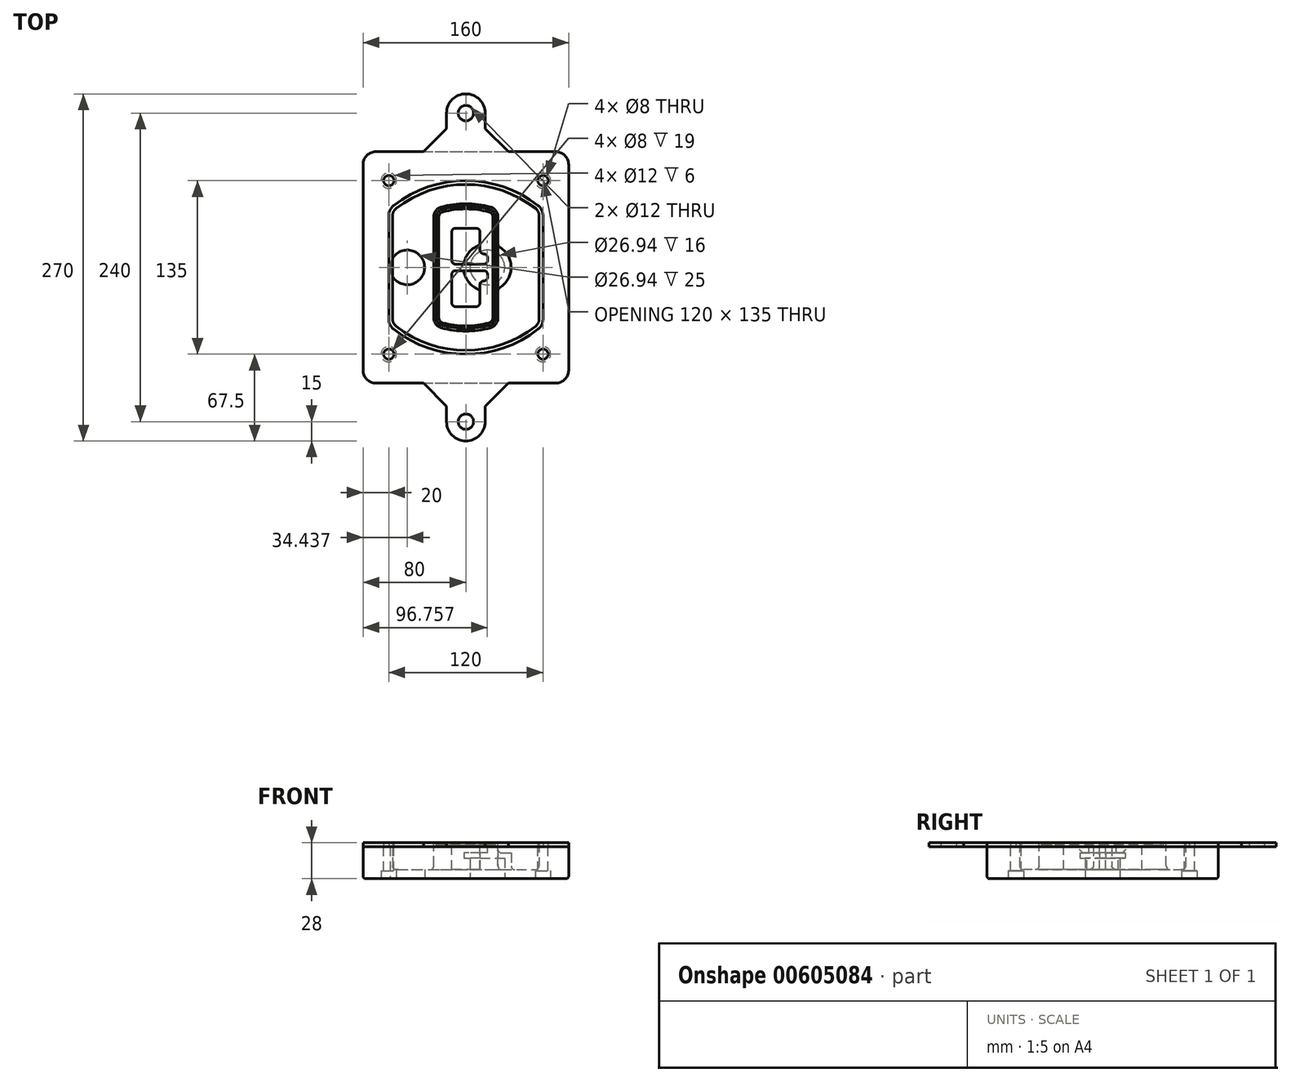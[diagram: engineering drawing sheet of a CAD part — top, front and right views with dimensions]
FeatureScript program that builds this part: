
annotation { "Feature Type Name" : "Feature", "Feature Type Description" : "" }
export const myFeature = defineFeature(function(context is Context, id is Id, definition is map)
    precondition{}
    {
        {
            var Q0;
            Q0=qCreatedBy(makeId("Top.planeOp"),FACE);
            var sketch = newSketch(context, id + "F0", { "sketchPlane" : qUnion([Q0])});
            skPoint(sketch, "E0.rect.middle", {"position": v(0, 0) * mm});
            skLineSegment(sketch, "E1.bottom", {"start": v(-70, -90) * mm, "end": v(70, -90) * mm});
            skLineSegment(sketch, "E1.top", {"start": v(-70, 90) * mm, "end": v(70, 90) * mm});
            skLineSegment(sketch, "E1.left", {"start": v(-80, -80) * mm, "end": v(-80, 80) * mm});
            skLineSegment(sketch, "E1.right", {"start": v(80, -80) * mm, "end": v(80, 80) * mm});
            skLineSegment(sketch, "E2", {"start": v(-80, 90) * mm, "end": v(80, -90) * mm, "construction": true});
            skLineSegment(sketch, "E3", {"start": v(80, 90) * mm, "end": v(-80, -90) * mm, "construction": true});
            skCircle(sketch, "E4", {"center": v(-60, 67.5) * mm, "radius": 4 * mm});
            skCircle(sketch, "E5", {"center": v(60, 67.5) * mm, "radius": 4 * mm});
            skCircle(sketch, "E6", {"center": v(60, -67.5) * mm, "radius": 4 * mm});
            skCircle(sketch, "E7", {"center": v(-60, -67.5) * mm, "radius": 4 * mm});
            skLineSegment(sketch, "E8", {"start": v(-60, 67.5) * mm, "end": v(60, 67.5) * mm, "construction": true});
            skLineSegment(sketch, "E9", {"start": v(60, 67.5) * mm, "end": v(60, -67.5) * mm, "construction": true});
            skLineSegment(sketch, "E10", {"start": v(60, -67.5) * mm, "end": v(-60, -67.5) * mm, "construction": true});
            skLineSegment(sketch, "E11", {"start": v(-60, -67.5) * mm, "end": v(-60, 67.5) * mm, "construction": true});
            skLineSegment(sketch, "E12", {"start": v(-60, 40.3) * mm, "end": v(-60, -40.3) * mm});
            skLineSegment(sketch, "E13", {"start": v(60, 40.3) * mm, "end": v(60, -40.3) * mm});
            skArc(sketch, "E14", {"start": v(56.15, 48.18) * mm, "mid": v(0, 67.5) * mm, "end": v(-56.15, 48.18) * mm});
            skArc(sketch, "E15", {"start": v(-56.15, -48.18) * mm, "mid": v(0, -67.5) * mm, "end": v(56.15, -48.18) * mm});
            skLineSegment(sketch, "E16", {"start": v(-60, 0) * mm, "end": v(60, 0) * mm, "construction": true});
            skPoint(sketch, "E17.visualSharp", {"position": v(-60, -45) * mm});
            skArc(sketch, "E17.filletArc", {"start": v(-60, -40.3) * mm, "mid": v(-58.99, -44.68) * mm, "end": v(-56.15, -48.18) * mm});
            skPoint(sketch, "E18.visualSharp", {"position": v(-60, 45) * mm});
            skArc(sketch, "E18.filletArc", {"start": v(-56.15, 48.18) * mm, "mid": v(-58.99, 44.68) * mm, "end": v(-60, 40.3) * mm});
            skPoint(sketch, "E19.visualSharp", {"position": v(60, 45) * mm});
            skArc(sketch, "E19.filletArc", {"start": v(60, 40.3) * mm, "mid": v(58.99, 44.68) * mm, "end": v(56.15, 48.18) * mm});
            skPoint(sketch, "E20.visualSharp", {"position": v(60, -45) * mm});
            skArc(sketch, "E20.filletArc", {"start": v(56.15, -48.18) * mm, "mid": v(58.99, -44.68) * mm, "end": v(60, -40.3) * mm});
            skPoint(sketch, "E21.visualSharp", {"position": v(-80, 90) * mm});
            skArc(sketch, "E21.filletArc", {"start": v(-70, 90) * mm, "mid": v(-77.07, 87.07) * mm, "end": v(-80, 80) * mm});
            skPoint(sketch, "E22.visualSharp", {"position": v(80, 90) * mm});
            skArc(sketch, "E22.filletArc", {"start": v(80, 80) * mm, "mid": v(77.07, 87.07) * mm, "end": v(70, 90) * mm});
            skPoint(sketch, "E23.visualSharp", {"position": v(80, -90) * mm});
            skArc(sketch, "E23.filletArc", {"start": v(70, -90) * mm, "mid": v(77.07, -87.07) * mm, "end": v(80, -80) * mm});
            skPoint(sketch, "E24.visualSharp", {"position": v(-80, -90) * mm});
            skArc(sketch, "E24.filletArc", {"start": v(-80, -80) * mm, "mid": v(-77.07, -87.07) * mm, "end": v(-70, -90) * mm});
            skArc(sketch, "E25.0", {"start": v(57, 40.3) * mm, "mid": v(56.3, 43.36) * mm, "end": v(54.3, 45.81) * mm});
            skLineSegment(sketch, "E25.1", {"start": v(57, 40.3) * mm, "end": v(57, -40.3) * mm});
            skArc(sketch, "E25.2", {"start": v(54.3, -45.81) * mm, "mid": v(56.3, -43.36) * mm, "end": v(57, -40.3) * mm});
            skArc(sketch, "E25.3", {"start": v(-54.3, -45.81) * mm, "mid": v(0, -64.5) * mm, "end": v(54.3, -45.81) * mm});
            skArc(sketch, "E25.4", {"start": v(-57, -40.3) * mm, "mid": v(-56.3, -43.36) * mm, "end": v(-54.3, -45.81) * mm});
            skArc(sketch, "E25.5", {"start": v(54.3, 45.81) * mm, "mid": v(0, 64.5) * mm, "end": v(-54.3, 45.81) * mm});
            skLineSegment(sketch, "E25.6", {"start": v(-57, 40.3) * mm, "end": v(-57, -40.3) * mm});
            skArc(sketch, "E25.7", {"start": v(-54.3, 45.81) * mm, "mid": v(-56.3, 43.36) * mm, "end": v(-57, 40.3) * mm});
            skArc(sketch, "E26.0", {"start": v(-58.62, 51.33) * mm, "mid": v(-62.58, 46.43) * mm, "end": v(-64, 40.3) * mm});
            skArc(sketch, "E26.1", {"start": v(58.62, 51.33) * mm, "mid": v(0, 71.5) * mm, "end": v(-58.62, 51.33) * mm});
            skArc(sketch, "E26.2", {"start": v(64, 40.3) * mm, "mid": v(62.58, 46.43) * mm, "end": v(58.62, 51.33) * mm});
            skLineSegment(sketch, "E26.3", {"start": v(64, 40.3) * mm, "end": v(64, -40.3) * mm});
            skArc(sketch, "E26.4", {"start": v(58.62, -51.33) * mm, "mid": v(62.58, -46.43) * mm, "end": v(64, -40.3) * mm});
            skLineSegment(sketch, "E26.5", {"start": v(-64, 40.3) * mm, "end": v(-64, -40.3) * mm});
            skArc(sketch, "E26.6", {"start": v(-58.62, -51.33) * mm, "mid": v(0, -71.5) * mm, "end": v(58.62, -51.33) * mm});
            skArc(sketch, "E26.7", {"start": v(-64, -40.3) * mm, "mid": v(-62.58, -46.43) * mm, "end": v(-58.62, -51.33) * mm});
            skSolve(sketch);
        }
        {
            var Q0;
            Q0=makeQuery(id+"F0.imprint","IMPRINT",FACE,{"disambiguationData":[TD([[makeQuery(id+"F0.imprint","IMPRINT",EDGE,{"derivedFrom":sQuery(id+"F0.wireOp",EDGE,"E1.bottom")}),1.0]])]});
            var Q1;
            Q1=makeQuery(id+"F0.imprint","IMPRINT",FACE,{"disambiguationData":[TD([[makeQuery(id+"F0.imprint","IMPRINT",EDGE,{"derivedFrom":sQuery(id+"F0.wireOp",EDGE,"E12")}),1.0]])]});
            var Q2;
            Q2=makeQuery(id+"F0.imprint","IMPRINT",FACE,{"disambiguationData":[TD([[makeQuery(id+"F0.imprint","IMPRINT",EDGE,{"derivedFrom":sQuery(id+"F0.wireOp",EDGE,"E25.0")}),1.0]])]});
            var Q3;
            Q3=makeQuery(id+"F0.imprint","IMPRINT",FACE,{"disambiguationData":[TD([[makeQuery(id+"F0.imprint","IMPRINT",EDGE,{"derivedFrom":sQuery(id+"F0.wireOp",EDGE,"E12")}),-1.0]])]});
            extrude(context, id + "F1", {"entities" : qUnion([Q0, Q1, Q2, Q3]), "oppositeDirection" : true, "depth" : 25 * mm});
        }
        {
            var Q0;
            Q0=makeQuery(id+"F0.imprint","IMPRINT",FACE,{"disambiguationData":[TD([[makeQuery(id+"F0.imprint","IMPRINT",EDGE,{"derivedFrom":sQuery(id+"F0.wireOp",EDGE,"E12")}),1.0]])]});
            extrude(context, id + "F2", {"entities" : qUnion([Q0]), "operationType" : NewBodyOperationType.ADD, "depth" : 3 * mm});
        }
        {
            var Q0;
            Q0=makeQuery(id+"F0.imprint","IMPRINT",FACE,{"disambiguationData":[TD([[makeQuery(id+"F0.imprint","IMPRINT",EDGE,{"derivedFrom":sQuery(id+"F0.wireOp",EDGE,"E25.0")}),1.0]])]});
            extrude(context, id + "F3", {"entities" : qUnion([Q0]), "operationType" : NewBodyOperationType.REMOVE, "oppositeDirection" : true, "depth" : 18 * mm});
        }
        {
            var Q0;
            Q0=makeQuery(id+"F2.opExtrude","CAP_FACE",FACE,{"disambiguationData":[OSD([sQuery(id+"F0.wireOp",EDGE,"E12"),sQuery(id+"F0.wireOp",EDGE,"E13"),sQuery(id+"F0.wireOp",EDGE,"E14"),sQuery(id+"F0.wireOp",EDGE,"E15"),sQuery(id+"F0.wireOp",EDGE,"E17.filletArc"),sQuery(id+"F0.wireOp",EDGE,"E18.filletArc"),sQuery(id+"F0.wireOp",EDGE,"E19.filletArc"),sQuery(id+"F0.wireOp",EDGE,"E20.filletArc"),sQuery(id+"F0.wireOp",EDGE,"E25.0"),sQuery(id+"F0.wireOp",EDGE,"E25.1"),sQuery(id+"F0.wireOp",EDGE,"E25.2"),sQuery(id+"F0.wireOp",EDGE,"E25.3"),sQuery(id+"F0.wireOp",EDGE,"E25.4"),sQuery(id+"F0.wireOp",EDGE,"E25.5"),sQuery(id+"F0.wireOp",EDGE,"E25.6"),sQuery(id+"F0.wireOp",EDGE,"E25.7")])],"isStart":false});
            var sketch = newSketch(context, id + "F4", { "sketchPlane" : qUnion([Q0])});
            skArc(sketch, "E27.0", {"start": v(-19.08, -46.97) * mm, "mid": v(0, -49.5) * mm, "end": v(19.08, -46.97) * mm});
            skArc(sketch, "E28.0", {"start": v(19.08, 46.97) * mm, "mid": v(0, 49.5) * mm, "end": v(-19.08, 46.97) * mm});
            skLineSegment(sketch, "E29", {"start": v(-25, 39.25) * mm, "end": v(-25, -39.25) * mm});
            skLineSegment(sketch, "E30", {"start": v(25, 39.25) * mm, "end": v(25, -39.25) * mm});
            skLineSegment(sketch, "E31", {"start": v(-25, 45.1) * mm, "end": v(25, 45.1) * mm, "construction": true});
            skLineSegment(sketch, "E32", {"start": v(-25, -45.1) * mm, "end": v(25, -45.1) * mm, "construction": true});
            skPoint(sketch, "E33.visualSharp", {"position": v(-25, 45.1) * mm});
            skArc(sketch, "E33.filletArc", {"start": v(-19.08, 46.97) * mm, "mid": v(-23.35, 44.11) * mm, "end": v(-25, 39.25) * mm});
            skPoint(sketch, "E34.visualSharp", {"position": v(25, 45.1) * mm});
            skArc(sketch, "E34.filletArc", {"start": v(25, 39.25) * mm, "mid": v(23.35, 44.11) * mm, "end": v(19.08, 46.97) * mm});
            skPoint(sketch, "E35.visualSharp", {"position": v(25, -45.1) * mm});
            skArc(sketch, "E35.filletArc", {"start": v(19.08, -46.97) * mm, "mid": v(23.35, -44.11) * mm, "end": v(25, -39.25) * mm});
            skPoint(sketch, "E36.visualSharp", {"position": v(-25, -45.1) * mm});
            skArc(sketch, "E36.filletArc", {"start": v(-25, -39.25) * mm, "mid": v(-23.35, -44.11) * mm, "end": v(-19.08, -46.97) * mm});
            skArc(sketch, "E37.0", {"start": v(54.3, 45.81) * mm, "mid": v(0, 64.5) * mm, "end": v(-54.3, 45.81) * mm});
            skArc(sketch, "E37.1", {"start": v(-54.3, 45.81) * mm, "mid": v(-56.3, 43.36) * mm, "end": v(-57, 40.3) * mm});
            skLineSegment(sketch, "E37.2", {"start": v(-57, 40.3) * mm, "end": v(-57, -40.3) * mm});
            skArc(sketch, "E37.3", {"start": v(-57, -40.3) * mm, "mid": v(-56.3, -43.36) * mm, "end": v(-54.3, -45.81) * mm});
            skArc(sketch, "E37.4", {"start": v(-54.3, -45.81) * mm, "mid": v(0, -64.5) * mm, "end": v(54.3, -45.81) * mm});
            skArc(sketch, "E37.5", {"start": v(54.3, -45.81) * mm, "mid": v(56.3, -43.36) * mm, "end": v(57, -40.3) * mm});
            skLineSegment(sketch, "E37.6", {"start": v(57, 40.3) * mm, "end": v(57, -40.3) * mm});
            skArc(sketch, "E37.7", {"start": v(57, 40.3) * mm, "mid": v(56.3, 43.36) * mm, "end": v(54.3, 45.81) * mm});
            skLineSegment(sketch, "E38.0", {"start": v(23, 39.25) * mm, "end": v(23, -39.25) * mm});
            skArc(sketch, "E38.1", {"start": v(18.56, -45.04) * mm, "mid": v(21.76, -42.9) * mm, "end": v(23, -39.25) * mm});
            skArc(sketch, "E38.2", {"start": v(-18.56, -45.04) * mm, "mid": v(0, -47.5) * mm, "end": v(18.56, -45.04) * mm});
            skArc(sketch, "E38.3", {"start": v(-23, -39.25) * mm, "mid": v(-21.76, -42.9) * mm, "end": v(-18.56, -45.04) * mm});
            skLineSegment(sketch, "E38.4", {"start": v(-23, 39.25) * mm, "end": v(-23, -39.25) * mm});
            skArc(sketch, "E38.5", {"start": v(23, 39.25) * mm, "mid": v(21.76, 42.9) * mm, "end": v(18.56, 45.04) * mm});
            skArc(sketch, "E38.6", {"start": v(-18.56, 45.04) * mm, "mid": v(-21.76, 42.9) * mm, "end": v(-23, 39.25) * mm});
            skArc(sketch, "E38.7", {"start": v(18.56, 45.04) * mm, "mid": v(0, 47.5) * mm, "end": v(-18.56, 45.04) * mm});
            skArc(sketch, "E39.0", {"start": v(21, 39.25) * mm, "mid": v(20.18, 41.68) * mm, "end": v(18.04, 43.1) * mm});
            skLineSegment(sketch, "E39.1", {"start": v(21, 39.25) * mm, "end": v(21, -39.25) * mm});
            skArc(sketch, "E39.2", {"start": v(18.04, -43.1) * mm, "mid": v(20.18, -41.68) * mm, "end": v(21, -39.25) * mm});
            skArc(sketch, "E39.3", {"start": v(-18.04, -43.1) * mm, "mid": v(0, -45.5) * mm, "end": v(18.04, -43.1) * mm});
            skArc(sketch, "E39.4", {"start": v(-21, -39.25) * mm, "mid": v(-20.18, -41.68) * mm, "end": v(-18.04, -43.1) * mm});
            skArc(sketch, "E39.5", {"start": v(18.04, 43.1) * mm, "mid": v(0, 45.5) * mm, "end": v(-18.04, 43.1) * mm});
            skLineSegment(sketch, "E39.6", {"start": v(-21, 39.25) * mm, "end": v(-21, -39.25) * mm});
            skArc(sketch, "E39.7", {"start": v(-18.04, 43.1) * mm, "mid": v(-20.18, 41.68) * mm, "end": v(-21, 39.25) * mm});
            skLineSegment(sketch, "E40", {"start": v(-25, 0) * mm, "end": v(25, 0) * mm, "construction": true});
            skLineSegment(sketch, "E41", {"start": v(-11, 5.5) * mm, "end": v(-11, 27.5) * mm});
            skLineSegment(sketch, "E42", {"start": v(-8, 30.5) * mm, "end": v(8, 30.5) * mm});
            skLineSegment(sketch, "E43", {"start": v(11, 27.5) * mm, "end": v(11, 13.5) * mm});
            skLineSegment(sketch, "E44", {"start": v(14, 10.5) * mm, "end": v(14, 10.5) * mm});
            skLineSegment(sketch, "E45", {"start": v(17, 7.5) * mm, "end": v(17, 5.5) * mm});
            skLineSegment(sketch, "E46", {"start": v(14, 2.5) * mm, "end": v(-8, 2.5) * mm});
            skPoint(sketch, "E47.visualSharp", {"position": v(-11, 30.5) * mm});
            skArc(sketch, "E47.filletArc", {"start": v(-8, 30.5) * mm, "mid": v(-10.12, 29.62) * mm, "end": v(-11, 27.5) * mm});
            skPoint(sketch, "E48.visualSharp", {"position": v(11, 30.5) * mm});
            skArc(sketch, "E48.filletArc", {"start": v(11, 27.5) * mm, "mid": v(10.12, 29.62) * mm, "end": v(8, 30.5) * mm});
            skPoint(sketch, "E49.visualSharp", {"position": v(11, 10.5) * mm});
            skArc(sketch, "E49.filletArc", {"start": v(11, 13.5) * mm, "mid": v(11.88, 11.38) * mm, "end": v(14, 10.5) * mm});
            skPoint(sketch, "E50.visualSharp", {"position": v(17, 10.5) * mm});
            skArc(sketch, "E50.filletArc", {"start": v(17, 7.5) * mm, "mid": v(16.12, 9.62) * mm, "end": v(14, 10.5) * mm});
            skPoint(sketch, "E51.visualSharp", {"position": v(17, 2.5) * mm});
            skArc(sketch, "E51.filletArc", {"start": v(14, 2.5) * mm, "mid": v(16.12, 3.38) * mm, "end": v(17, 5.5) * mm});
            skPoint(sketch, "E52.visualSharp", {"position": v(-11, 2.5) * mm});
            skArc(sketch, "E52.filletArc", {"start": v(-11, 5.5) * mm, "mid": v(-10.12, 3.38) * mm, "end": v(-8, 2.5) * mm});
            skLineSegment(sketch, "E53.0.MirrorCS", {"start": v(14, -2.5) * mm, "end": v(-8, -2.5) * mm});
            skArc(sketch, "E54.0.MirrorCS", {"start": v(-11, -5.5) * mm, "mid": v(-10.12, -3.38) * mm, "end": v(-8, -2.5) * mm});
            skLineSegment(sketch, "E55.0.MirrorCS", {"start": v(-11, -5.5) * mm, "end": v(-11, -27.5) * mm});
            skArc(sketch, "E56.0.MirrorCS", {"start": v(-8, -30.5) * mm, "mid": v(-10.12, -29.62) * mm, "end": v(-11, -27.5) * mm});
            skLineSegment(sketch, "E57.0.MirrorCS", {"start": v(-8, -30.5) * mm, "end": v(8, -30.5) * mm});
            skArc(sketch, "E58.0.MirrorCS", {"start": v(11, -27.5) * mm, "mid": v(10.12, -29.62) * mm, "end": v(8, -30.5) * mm});
            skLineSegment(sketch, "E59.0.MirrorCS", {"start": v(11, -27.5) * mm, "end": v(11, -13.5) * mm});
            skArc(sketch, "E60.0.MirrorCS", {"start": v(11, -13.5) * mm, "mid": v(11.88, -11.38) * mm, "end": v(14, -10.5) * mm});
            skArc(sketch, "E61.0.MirrorCS", {"start": v(17, -7.5) * mm, "mid": v(16.12, -9.62) * mm, "end": v(14, -10.5) * mm});
            skLineSegment(sketch, "E62.0.MirrorCS", {"start": v(17, -7.5) * mm, "end": v(17, -5.5) * mm});
            skArc(sketch, "E63.0.MirrorCS", {"start": v(14, -2.5) * mm, "mid": v(16.12, -3.38) * mm, "end": v(17, -5.5) * mm});
            skSolve(sketch);
        }
        {
            var Q0;
            Q0=makeQuery(id+"F4.imprint","IMPRINT",FACE,{"disambiguationData":[TD([[makeQuery(id+"F4.imprint","IMPRINT",EDGE,{"derivedFrom":sQuery(id+"F4.wireOp",EDGE,"E27.0")}),1.0]])]});
            var Q1;
            Q1=makeQuery(id+"F4.imprint","IMPRINT",FACE,{"disambiguationData":[TD([[makeQuery(id+"F4.imprint","IMPRINT",EDGE,{"derivedFrom":sQuery(id+"F4.wireOp",EDGE,"E38.0")}),-1.0]])]});
            var Q2;
            Q2=makeQuery(id+"F4.imprint","IMPRINT",FACE,{"disambiguationData":[TD([[makeQuery(id+"F4.imprint","IMPRINT",EDGE,{"derivedFrom":sQuery(id+"F4.wireOp",EDGE,"E39.0")}),1.0]])]});
            extrude(context, id + "F5", {"entities" : qUnion([Q0, Q1, Q2]), "operationType" : NewBodyOperationType.ADD, "endBound" : BoundingType.UP_TO_NEXT, "oppositeDirection" : true, "depth" : 25 * mm});
        }
        {
            var Q0;
            Q0=makeQuery(id+"F4.imprint","IMPRINT",FACE,{"disambiguationData":[TD([[makeQuery(id+"F4.imprint","IMPRINT",EDGE,{"derivedFrom":sQuery(id+"F4.wireOp",EDGE,"E38.0")}),-1.0]])]});
            extrude(context, id + "F6", {"entities" : qUnion([Q0]), "operationType" : NewBodyOperationType.REMOVE, "oppositeDirection" : true, "depth" : 2 * mm});
        }
        {
            var Q0;
            Q0=makeQuery(id+"F1.opExtrude","CAP_FACE",FACE,{"disambiguationData":[OSD([sQuery(id+"F0.wireOp",EDGE,"E1.bottom"),sQuery(id+"F0.wireOp",EDGE,"E1.top"),sQuery(id+"F0.wireOp",EDGE,"E1.left"),sQuery(id+"F0.wireOp",EDGE,"E1.right"),sQuery(id+"F0.wireOp",EDGE,"E4"),sQuery(id+"F0.wireOp",EDGE,"E5"),sQuery(id+"F0.wireOp",EDGE,"E6"),sQuery(id+"F0.wireOp",EDGE,"E7"),sQuery(id+"F0.wireOp",EDGE,"E21.filletArc"),sQuery(id+"F0.wireOp",EDGE,"E22.filletArc"),sQuery(id+"F0.wireOp",EDGE,"E23.filletArc"),sQuery(id+"F0.wireOp",EDGE,"E24.filletArc")])],"isStart":false});
            var sketch = newSketch(context, id + "F7", { "sketchPlane" : qUnion([Q0])});
            skCircle(sketch, "E64", {"center": v(16.76, 0) * mm, "radius": 13.47 * mm});
            skCircle(sketch, "E65", {"center": v(-45.56, 0) * mm, "radius": 13.47 * mm});
            skLineSegment(sketch, "E66", {"start": v(80, 0) * mm, "end": v(-80, 0) * mm});
            skCircle(sketch, "E67", {"center": v(16.76, 0) * mm, "radius": 18.47 * mm});
            skCircle(sketch, "E68", {"center": v(60, -67.5) * mm, "radius": 6 * mm});
            skCircle(sketch, "E69", {"center": v(-60, -67.5) * mm, "radius": 6 * mm});
            skCircle(sketch, "E70", {"center": v(-60, 67.5) * mm, "radius": 6 * mm});
            skCircle(sketch, "E71", {"center": v(60, 67.5) * mm, "radius": 6 * mm});
            skSolve(sketch);
        }
        {
            var Q0;
            {var subQ1=sQuery(id+"F7.wireOp",EDGE,"E66");var subQ4=sQuery(id+"F7.wireOp",EDGE,"E64");var subQ6=makeQuery(id+"F7.imprint","INTERSECT",VERTEX,{"disambiguationData":[OD(0.0)],"derivedFrom":[subQ4,subQ1]});Q0=makeQuery(id+"F7.imprint","IMPRINT",FACE,{"disambiguationData":[TD([[makeQuery(id+"F7.imprint","IMPRINT",EDGE,{"disambiguationData":[TD([[subQ6,-1.0]])],"derivedFrom":subQ4}),-1.0]])]});}
            var Q1;
            {var subQ0=sQuery(id+"F7.wireOp",EDGE,"E66");var subQ1=sQuery(id+"F7.wireOp",EDGE,"E64");var subQ3=makeQuery(id+"F7.imprint","INTERSECT",VERTEX,{"disambiguationData":[OD(0.0)],"derivedFrom":[subQ1,subQ0]});Q1=makeQuery(id+"F7.imprint","IMPRINT",FACE,{"disambiguationData":[TD([[makeQuery(id+"F7.imprint","IMPRINT",EDGE,{"disambiguationData":[TD([[subQ3,-1.0]])],"derivedFrom":subQ1}),1.0]])]});}
            var Q2;
            {var subQ0=sQuery(id+"F7.wireOp",EDGE,"E66");var subQ1=sQuery(id+"F7.wireOp",EDGE,"E64");var subQ3=makeQuery(id+"F7.imprint","INTERSECT",VERTEX,{"disambiguationData":[OD(0.0)],"derivedFrom":[subQ1,subQ0]});Q2=makeQuery(id+"F7.imprint","IMPRINT",FACE,{"disambiguationData":[TD([[makeQuery(id+"F7.imprint","IMPRINT",EDGE,{"disambiguationData":[TD([[subQ3,1.0]])],"derivedFrom":subQ1}),1.0]])]});}
            var Q3;
            {var subQ1=sQuery(id+"F7.wireOp",EDGE,"E66");var subQ4=sQuery(id+"F7.wireOp",EDGE,"E64");var subQ6=makeQuery(id+"F7.imprint","INTERSECT",VERTEX,{"disambiguationData":[OD(0.0)],"derivedFrom":[subQ4,subQ1]});Q3=makeQuery(id+"F7.imprint","IMPRINT",FACE,{"disambiguationData":[TD([[makeQuery(id+"F7.imprint","IMPRINT",EDGE,{"disambiguationData":[TD([[subQ6,1.0]])],"derivedFrom":subQ4}),-1.0]])]});}
            extrude(context, id + "F8", {"entities" : qUnion([Q0, Q1, Q2, Q3]), "operationType" : NewBodyOperationType.ADD, "oppositeDirection" : true, "depth" : 20 * mm});
        }
        {
            var Q0;
            {var subQ0=sQuery(id+"F7.wireOp",EDGE,"E66");var subQ1=sQuery(id+"F7.wireOp",EDGE,"E64");var subQ3=makeQuery(id+"F7.imprint","INTERSECT",VERTEX,{"disambiguationData":[OD(0.0)],"derivedFrom":[subQ1,subQ0]});Q0=makeQuery(id+"F7.imprint","IMPRINT",FACE,{"disambiguationData":[TD([[makeQuery(id+"F7.imprint","IMPRINT",EDGE,{"disambiguationData":[TD([[subQ3,-1.0]])],"derivedFrom":subQ1}),1.0]])]});}
            var Q1;
            {var subQ0=sQuery(id+"F7.wireOp",EDGE,"E66");var subQ1=sQuery(id+"F7.wireOp",EDGE,"E64");var subQ3=makeQuery(id+"F7.imprint","INTERSECT",VERTEX,{"disambiguationData":[OD(0.0)],"derivedFrom":[subQ1,subQ0]});Q1=makeQuery(id+"F7.imprint","IMPRINT",FACE,{"disambiguationData":[TD([[makeQuery(id+"F7.imprint","IMPRINT",EDGE,{"disambiguationData":[TD([[subQ3,1.0]])],"derivedFrom":subQ1}),1.0]])]});}
            extrude(context, id + "F9", {"entities" : qUnion([Q0, Q1]), "operationType" : NewBodyOperationType.REMOVE, "oppositeDirection" : true, "depth" : 16 * mm});
        }
        {
            var Q0;
            {var subQ0=sQuery(id+"F7.wireOp",EDGE,"E66");var subQ1=sQuery(id+"F7.wireOp",EDGE,"E65");var subQ3=makeQuery(id+"F7.imprint","INTERSECT",VERTEX,{"disambiguationData":[OD(0.0)],"derivedFrom":[subQ1,subQ0]});Q0=makeQuery(id+"F7.imprint","IMPRINT",FACE,{"disambiguationData":[TD([[makeQuery(id+"F7.imprint","IMPRINT",EDGE,{"disambiguationData":[TD([[subQ3,-1.0]])],"derivedFrom":subQ1}),1.0]])]});}
            var Q1;
            {var subQ0=sQuery(id+"F7.wireOp",EDGE,"E66");var subQ1=sQuery(id+"F7.wireOp",EDGE,"E65");var subQ3=makeQuery(id+"F7.imprint","INTERSECT",VERTEX,{"disambiguationData":[OD(0.0)],"derivedFrom":[subQ1,subQ0]});Q1=makeQuery(id+"F7.imprint","IMPRINT",FACE,{"disambiguationData":[TD([[makeQuery(id+"F7.imprint","IMPRINT",EDGE,{"disambiguationData":[TD([[subQ3,1.0]])],"derivedFrom":subQ1}),1.0]])]});}
            extrude(context, id + "F10", {"entities" : qUnion([Q0, Q1]), "operationType" : NewBodyOperationType.REMOVE, "oppositeDirection" : true, "depth" : 25 * mm});
        }
        {
            var Q0;
            Q0=makeQuery(id+"F7.imprint","IMPRINT",FACE,{"disambiguationData":[TD([[makeQuery(id+"F7.imprint","IMPRINT",EDGE,{"derivedFrom":sQuery(id+"F7.wireOp",EDGE,"E68")}),1.0]])]});
            var Q1;
            Q1=makeQuery(id+"F7.imprint","IMPRINT",FACE,{"disambiguationData":[TD([[makeQuery(id+"F7.imprint","IMPRINT",EDGE,{"derivedFrom":makeQuery(id+"F1.opExtrude","CAP_EDGE",EDGE,{"disambiguationData":[OSD([sQuery(id+"F0.wireOp",EDGE,"E5")])],"isStart":false})}),-1.0]])]});
            var Q2;
            Q2=makeQuery(id+"F7.imprint","IMPRINT",FACE,{"disambiguationData":[TD([[makeQuery(id+"F7.imprint","IMPRINT",EDGE,{"derivedFrom":sQuery(id+"F7.wireOp",EDGE,"E69")}),1.0]])]});
            var Q3;
            Q3=makeQuery(id+"F7.imprint","IMPRINT",FACE,{"disambiguationData":[TD([[makeQuery(id+"F7.imprint","IMPRINT",EDGE,{"derivedFrom":makeQuery(id+"F1.opExtrude","CAP_EDGE",EDGE,{"disambiguationData":[OSD([sQuery(id+"F0.wireOp",EDGE,"E4")])],"isStart":false})}),-1.0]])]});
            var Q4;
            Q4=makeQuery(id+"F7.imprint","IMPRINT",FACE,{"disambiguationData":[TD([[makeQuery(id+"F7.imprint","IMPRINT",EDGE,{"derivedFrom":sQuery(id+"F7.wireOp",EDGE,"E70")}),1.0]])]});
            var Q5;
            Q5=makeQuery(id+"F7.imprint","IMPRINT",FACE,{"disambiguationData":[TD([[makeQuery(id+"F7.imprint","IMPRINT",EDGE,{"derivedFrom":makeQuery(id+"F1.opExtrude","CAP_EDGE",EDGE,{"disambiguationData":[OSD([sQuery(id+"F0.wireOp",EDGE,"E7")])],"isStart":false})}),-1.0]])]});
            var Q6;
            Q6=makeQuery(id+"F7.imprint","IMPRINT",FACE,{"disambiguationData":[TD([[makeQuery(id+"F7.imprint","IMPRINT",EDGE,{"derivedFrom":sQuery(id+"F7.wireOp",EDGE,"E71")}),1.0]])]});
            var Q7;
            Q7=makeQuery(id+"F7.imprint","IMPRINT",FACE,{"disambiguationData":[TD([[makeQuery(id+"F7.imprint","IMPRINT",EDGE,{"derivedFrom":makeQuery(id+"F1.opExtrude","CAP_EDGE",EDGE,{"disambiguationData":[OSD([sQuery(id+"F0.wireOp",EDGE,"E6")])],"isStart":false})}),-1.0]])]});
            extrude(context, id + "F11", {"entities" : qUnion([Q0, Q1, Q2, Q3, Q4, Q5, Q6, Q7]), "operationType" : NewBodyOperationType.REMOVE, "oppositeDirection" : true, "depth" : 6 * mm});
        }
        {
            var Q0;
            Q0=makeQuery(id+"F9.boolean.opBoolean","COPY",FACE,{"derivedFrom":makeQuery(id+"F9.opExtrude","CAP_FACE",FACE,{"disambiguationData":[OSD([sQuery(id+"F7.wireOp",EDGE,"E64")])],"isStart":false})});
            var sketch = newSketch(context, id + "F12", { "sketchPlane" : qUnion([Q0])});
            skArc(sketch, "E72.0", {"start": v(11, 17.55) * mm, "mid": v(2.57, 11.82) * mm, "end": v(-1.54, 2.5) * mm});
            skArc(sketch, "E72.1", {"start": v(-1.54, -2.5) * mm, "mid": v(2.57, -11.82) * mm, "end": v(11, -17.55) * mm});
            skLineSegment(sketch, "E73", {"start": v(-1.54, -2.5) * mm, "end": v(14, -2.5) * mm});
            skLineSegment(sketch, "E74.0", {"start": v(14, 2.5) * mm, "end": v(-1.54, 2.5) * mm});
            skArc(sketch, "E74.1", {"start": v(14, 2.5) * mm, "mid": v(16.12, 3.38) * mm, "end": v(17, 5.5) * mm});
            skLineSegment(sketch, "E74.2", {"start": v(17, 7.5) * mm, "end": v(17, 5.5) * mm});
            skArc(sketch, "E74.3", {"start": v(17, 7.5) * mm, "mid": v(16.12, 9.62) * mm, "end": v(14, 10.5) * mm});
            skArc(sketch, "E74.4", {"start": v(11, 13.5) * mm, "mid": v(11.88, 11.38) * mm, "end": v(14, 10.5) * mm});
            skLineSegment(sketch, "E74.5", {"start": v(11, 17.55) * mm, "end": v(11, 13.5) * mm});
            skLineSegment(sketch, "E74.7", {"start": v(14, -2.5) * mm, "end": v(-1.54, -2.5) * mm});
            skArc(sketch, "E74.8", {"start": v(14, -2.5) * mm, "mid": v(16.12, -3.38) * mm, "end": v(17, -5.5) * mm});
            skLineSegment(sketch, "E74.9", {"start": v(17, -7.5) * mm, "end": v(17, -5.5) * mm});
            skArc(sketch, "E74.10", {"start": v(17, -7.5) * mm, "mid": v(16.12, -9.62) * mm, "end": v(14, -10.5) * mm});
            skArc(sketch, "E74.11", {"start": v(11, -13.5) * mm, "mid": v(11.88, -11.38) * mm, "end": v(14, -10.5) * mm});
            skLineSegment(sketch, "E74.12", {"start": v(11, -17.55) * mm, "end": v(11, -13.5) * mm});
            skPoint(sketch, "E75.orphan", {"position": v(11, -27.5) * mm});
            skPoint(sketch, "E76.orphan", {"position": v(-8, -2.5) * mm});
            skPoint(sketch, "E77.orphan", {"position": v(-8, 2.5) * mm});
            skPoint(sketch, "E78.orphan", {"position": v(11, 27.5) * mm});
            skSolve(sketch);
        }
        {
            var Q0;
            {var subQ7=sQuery(id+"F12.wireOp",EDGE,"E72.0");var subQ14=sQuery(id+"F12.wireOp",EDGE,"E72.1");var subQ16=sQuery(id+"F12.wireOp",EDGE,"E74.1");var subQ18=sQuery(id+"F12.wireOp",EDGE,"E74.8");Q0=qUnion([makeQuery(id+"F12.imprint","IMPRINT",FACE,{"disambiguationData":[TD([[makeQuery(id+"F12.imprint","IMPRINT",EDGE,{"derivedFrom":subQ7}),1.0]])]}),makeQuery(id+"F12.imprint","IMPRINT",FACE,{"disambiguationData":[TD([[makeQuery(id+"F12.imprint","IMPRINT",EDGE,{"derivedFrom":subQ14}),1.0]])]}),makeQuery(id+"F12.imprint","IMPRINT",FACE,{"disambiguationData":[TD([[makeQuery(id+"F12.imprint","IMPRINT",EDGE,{"derivedFrom":subQ16}),1.0]])]}),makeQuery(id+"F12.imprint","IMPRINT",FACE,{"disambiguationData":[TD([[makeQuery(id+"F12.imprint","IMPRINT",EDGE,{"derivedFrom":subQ18}),-1.0]])]})]);}
            var Q1;
            Q1=makeQuery(id+"F5.boolean.opBoolean","SPLIT",FACE,{"disambiguationData":[TD([makeQuery(id+"F5.opExtrude","SWEPT_FACE",FACE,{"disambiguationData":[OSD([sQuery(id+"F4.wireOp",EDGE,"E41")])]})])],"derivedFrom":makeQuery(id+"F3.boolean.opBoolean","COPY",FACE,{"derivedFrom":makeQuery(id+"F3.opExtrude","CAP_FACE",FACE,{"disambiguationData":[OSD([sQuery(id+"F0.wireOp",EDGE,"E25.0"),sQuery(id+"F0.wireOp",EDGE,"E25.1"),sQuery(id+"F0.wireOp",EDGE,"E25.2"),sQuery(id+"F0.wireOp",EDGE,"E25.3"),sQuery(id+"F0.wireOp",EDGE,"E25.4"),sQuery(id+"F0.wireOp",EDGE,"E25.5"),sQuery(id+"F0.wireOp",EDGE,"E25.6"),sQuery(id+"F0.wireOp",EDGE,"E25.7")])],"isStart":false})})});
            extrude(context, id + "F13", {"entities" : qUnion([Q0]), "operationType" : NewBodyOperationType.REMOVE, "endBound" : BoundingType.UP_TO_SURFACE, "endBoundEntityFace" : qUnion([Q1]), "depth" : 25 * mm});
        }
        {
            var Q0;
            Q0=makeQuery(id+"F3.boolean.opBoolean","COPY",EDGE,{"derivedFrom":makeQuery(id+"F3.opExtrude","CAP_EDGE",EDGE,{"disambiguationData":[OSD([sQuery(id+"F0.wireOp",EDGE,"E25.6")])],"isStart":false})});
            var Q1;
            Q1=makeQuery(id+"F8.boolean.opBoolean","INTERSECT",EDGE,{"derivedFrom":[makeQuery(id+"F5.opExtrude","SWEPT_FACE",FACE,{"disambiguationData":[OSD([sQuery(id+"F4.wireOp",EDGE,"E30")])]}),makeQuery(id+"F8.opExtrude","CAP_FACE",FACE,{"disambiguationData":[OSD([sQuery(id+"F7.wireOp",EDGE,"E67")])],"isStart":false})]});
            var Q2;
            Q2=makeQuery(id+"F8.boolean.opBoolean","INTERSECT",EDGE,{"disambiguationData":[OD(1.0)],"derivedFrom":[makeQuery(id+"F5.opExtrude","SWEPT_FACE",FACE,{"disambiguationData":[OSD([sQuery(id+"F4.wireOp",EDGE,"E30")])]}),makeQuery(id+"F8.opExtrude","SWEPT_FACE",FACE,{"disambiguationData":[OSD([sQuery(id+"F7.wireOp",EDGE,"E67")])]})]});
            var Q3;
            {var subQ0=sQuery(id+"F4.wireOp",EDGE,"E30");Q3=makeQuery(id+"F8.boolean.opBoolean","SPLIT",EDGE,{"disambiguationData":[TD([makeQuery(id+"F5.opExtrude","SWEPT_FACE",FACE,{"disambiguationData":[OSD([sQuery(id+"F4.wireOp",EDGE,"E35.filletArc")])]})])],"derivedFrom":makeQuery(id+"F5.opExtrude","CAP_EDGE",EDGE,{"disambiguationData":[OSD([subQ0])],"isStart":false})});}
            var Q4;
            {var subQ0=sQuery(id+"F0.wireOp",EDGE,"E25.7");var subQ1=sQuery(id+"F0.wireOp",EDGE,"E25.1");var subQ2=sQuery(id+"F0.wireOp",EDGE,"E25.6");var subQ3=sQuery(id+"F0.wireOp",EDGE,"E25.5");var subQ4=sQuery(id+"F0.wireOp",EDGE,"E25.4");var subQ5=sQuery(id+"F0.wireOp",EDGE,"E25.0");var subQ6=sQuery(id+"F0.wireOp",EDGE,"E25.2");var subQ7=sQuery(id+"F0.wireOp",EDGE,"E25.3");Q4=makeQuery(id+"F8.boolean.opBoolean","INTERSECT",EDGE,{"derivedFrom":[makeQuery(id+"F5.boolean.opBoolean","SPLIT",FACE,{"disambiguationData":[TD([makeQuery(id+"F2.opExtrude","SWEPT_FACE",FACE,{"disambiguationData":[OSD([subQ5])]})])],"derivedFrom":makeQuery(id+"F3.boolean.opBoolean","COPY",FACE,{"derivedFrom":makeQuery(id+"F3.opExtrude","CAP_FACE",FACE,{"disambiguationData":[OSD([subQ5,subQ1,subQ6,subQ7,subQ4,subQ3,subQ2,subQ0])],"isStart":false})})}),makeQuery(id+"F8.opExtrude","SWEPT_FACE",FACE,{"disambiguationData":[OSD([sQuery(id+"F7.wireOp",EDGE,"E67")])]})]});}
            var Q5;
            Q5=makeQuery(id+"F8.boolean.opBoolean","INTERSECT",EDGE,{"disambiguationData":[OD(0.0)],"derivedFrom":[makeQuery(id+"F5.opExtrude","SWEPT_FACE",FACE,{"disambiguationData":[OSD([sQuery(id+"F4.wireOp",EDGE,"E30")])]}),makeQuery(id+"F8.opExtrude","SWEPT_FACE",FACE,{"disambiguationData":[OSD([sQuery(id+"F7.wireOp",EDGE,"E67")])]})]});
            fillet(context, id + "F14", {"entities" : qUnion([Q0, Q1, Q2, Q3, Q4, Q5]), "radius" : 3 * mm, "tangentPropagation" : true, "allowEdgeOverflow" : false});
        }
        {
            var Q0;
            Q0=makeQuery(id+"F1.opExtrude","CAP_EDGE",EDGE,{"disambiguationData":[OSD([sQuery(id+"F0.wireOp",EDGE,"E1.bottom")])],"isStart":false});
            fillet(context, id + "F15", {"entities" : qUnion([Q0]), "radius" : 2 * mm, "tangentPropagation" : true, "allowEdgeOverflow" : false});
        }
        {
            var Q0;
            {var subQ0=sQuery(id+"F0.wireOp",EDGE,"E21.filletArc");var subQ1=sQuery(id+"F0.wireOp",EDGE,"E7");var subQ2=sQuery(id+"F0.wireOp",EDGE,"E6");var subQ3=sQuery(id+"F0.wireOp",EDGE,"E5");var subQ4=sQuery(id+"F0.wireOp",EDGE,"E4");var subQ5=sQuery(id+"F0.wireOp",EDGE,"E22.filletArc");var subQ6=sQuery(id+"F0.wireOp",EDGE,"E1.bottom");var subQ7=sQuery(id+"F0.wireOp",EDGE,"E1.right");var subQ8=sQuery(id+"F0.wireOp",EDGE,"E1.top");var subQ9=sQuery(id+"F0.wireOp",EDGE,"E1.left");var subQ10=sQuery(id+"F0.wireOp",EDGE,"E23.filletArc");var subQ11=sQuery(id+"F0.wireOp",EDGE,"E24.filletArc");Q0=makeQuery(id+"F2.boolean.opBoolean","SPLIT",FACE,{"disambiguationData":[TD([makeQuery(id+"F1.opExtrude","SWEPT_FACE",FACE,{"disambiguationData":[OSD([subQ6])]})])],"derivedFrom":makeQuery(id+"F1.opExtrude","CAP_FACE",FACE,{"disambiguationData":[OSD([subQ6,subQ8,subQ9,subQ7,subQ4,subQ3,subQ2,subQ1,subQ0,subQ5,subQ10,subQ11])],"isStart":true})});}
            var sketch = newSketch(context, id + "F16", { "sketchPlane" : qUnion([Q0])});
            skLineSegment(sketch, "E79", {"start": v(0, 90) * mm, "end": v(0, 120) * mm, "construction": true});
            skLineSegment(sketch, "E80", {"start": v(0, 90) * mm, "end": v(15, 90) * mm, "construction": true});
            skLineSegment(sketch, "E81", {"start": v(0, 90) * mm, "end": v(-15, 90) * mm, "construction": true});
            skLineSegment(sketch, "E82", {"start": v(-15, 90) * mm, "end": v(-15, 108) * mm, "construction": true});
            skLineSegment(sketch, "E83", {"start": v(15, 90) * mm, "end": v(15, 108) * mm, "construction": true});
            skLineSegment(sketch, "E84", {"start": v(-15, 108) * mm, "end": v(-15, 120) * mm});
            skLineSegment(sketch, "E85", {"start": v(15, 108) * mm, "end": v(15, 120) * mm});
            skArc(sketch, "E86", {"start": v(-15, 120) * mm, "mid": v(0, 135) * mm, "end": v(15, 120) * mm});
            skLineSegment(sketch, "E87", {"start": v(-15, 108) * mm, "end": v(-33, 90) * mm});
            skLineSegment(sketch, "E88", {"start": v(15, 108) * mm, "end": v(33, 90) * mm});
            skCircle(sketch, "E89", {"center": v(0, 120) * mm, "radius": 6 * mm});
            skLineSegment(sketch, "E90", {"start": v(0, 0) * mm, "end": v(176, 0) * mm, "construction": true});
            skPoint(sketch, "E90.endSnap0", {"position": v(80, 0) * mm});
            skLineSegment(sketch, "E91", {"start": v(176, 0) * mm, "end": v(-93.95, 0) * mm, "construction": true});
            skPoint(sketch, "E91.endSnap0", {"position": v(-80, 0) * mm});
            skLineSegment(sketch, "E92.MirrorCS", {"start": v(-15, -108) * mm, "end": v(-33, -90) * mm});
            skLineSegment(sketch, "E93.MirrorCS", {"start": v(-15, -108) * mm, "end": v(-15, -120) * mm});
            skArc(sketch, "E94.MirrorCS", {"start": v(-15, -120) * mm, "mid": v(0, -135) * mm, "end": v(15, -120) * mm});
            skLineSegment(sketch, "E95.MirrorCS", {"start": v(15, -108) * mm, "end": v(15, -120) * mm});
            skLineSegment(sketch, "E96.MirrorCS", {"start": v(15, -108) * mm, "end": v(33, -90) * mm});
            skCircle(sketch, "E97.MirrorC", {"center": v(0, -120) * mm, "radius": 6 * mm});
            skSolve(sketch);
        }
        {
            var Q0;
            {var subQ0=sQuery(id+"F16.wireOp",EDGE,"E92.MirrorCS");Q0=makeQuery(id+"F16.imprint","IMPRINT",FACE,{"disambiguationData":[TD([[makeQuery(id+"F16.imprint","IMPRINT",EDGE,{"derivedFrom":subQ0}),-1.0]])]});}
            var Q1;
            Q1=makeQuery(id+"F16.imprint","IMPRINT",FACE,{"disambiguationData":[TD([[makeQuery(id+"F16.imprint","IMPRINT",EDGE,{"derivedFrom":sQuery(id+"F16.wireOp",EDGE,"E84")}),-1.0]])]});
            var Q2;
            Q2=makeQuery(id+"F16.imprint","IMPRINT",FACE,{"disambiguationData":[TD([[makeQuery(id+"F16.imprint","IMPRINT",EDGE,{"derivedFrom":makeQuery(id+"F1.opExtrude","CAP_EDGE",EDGE,{"disambiguationData":[OSD([sQuery(id+"F0.wireOp",EDGE,"E1.left")])],"isStart":true})}),-1.0]])]});
            var Q3;
            Q3=makeQuery(id+"F2.opExtrude","CAP_FACE",FACE,{"disambiguationData":[OSD([sQuery(id+"F0.wireOp",EDGE,"E12"),sQuery(id+"F0.wireOp",EDGE,"E13"),sQuery(id+"F0.wireOp",EDGE,"E14"),sQuery(id+"F0.wireOp",EDGE,"E15"),sQuery(id+"F0.wireOp",EDGE,"E17.filletArc"),sQuery(id+"F0.wireOp",EDGE,"E18.filletArc"),sQuery(id+"F0.wireOp",EDGE,"E19.filletArc"),sQuery(id+"F0.wireOp",EDGE,"E20.filletArc"),sQuery(id+"F0.wireOp",EDGE,"E25.0"),sQuery(id+"F0.wireOp",EDGE,"E25.1"),sQuery(id+"F0.wireOp",EDGE,"E25.2"),sQuery(id+"F0.wireOp",EDGE,"E25.3"),sQuery(id+"F0.wireOp",EDGE,"E25.4"),sQuery(id+"F0.wireOp",EDGE,"E25.5"),sQuery(id+"F0.wireOp",EDGE,"E25.6"),sQuery(id+"F0.wireOp",EDGE,"E25.7")])],"isStart":false});
            extrude(context, id + "F17", {"entities" : qUnion([Q0, Q1, Q2]), "endBound" : BoundingType.UP_TO_SURFACE, "depth" : 25 * mm, "endBoundEntityFace" : qUnion([Q3]), "offsetDistance" : 25 * mm});
        }
    });
